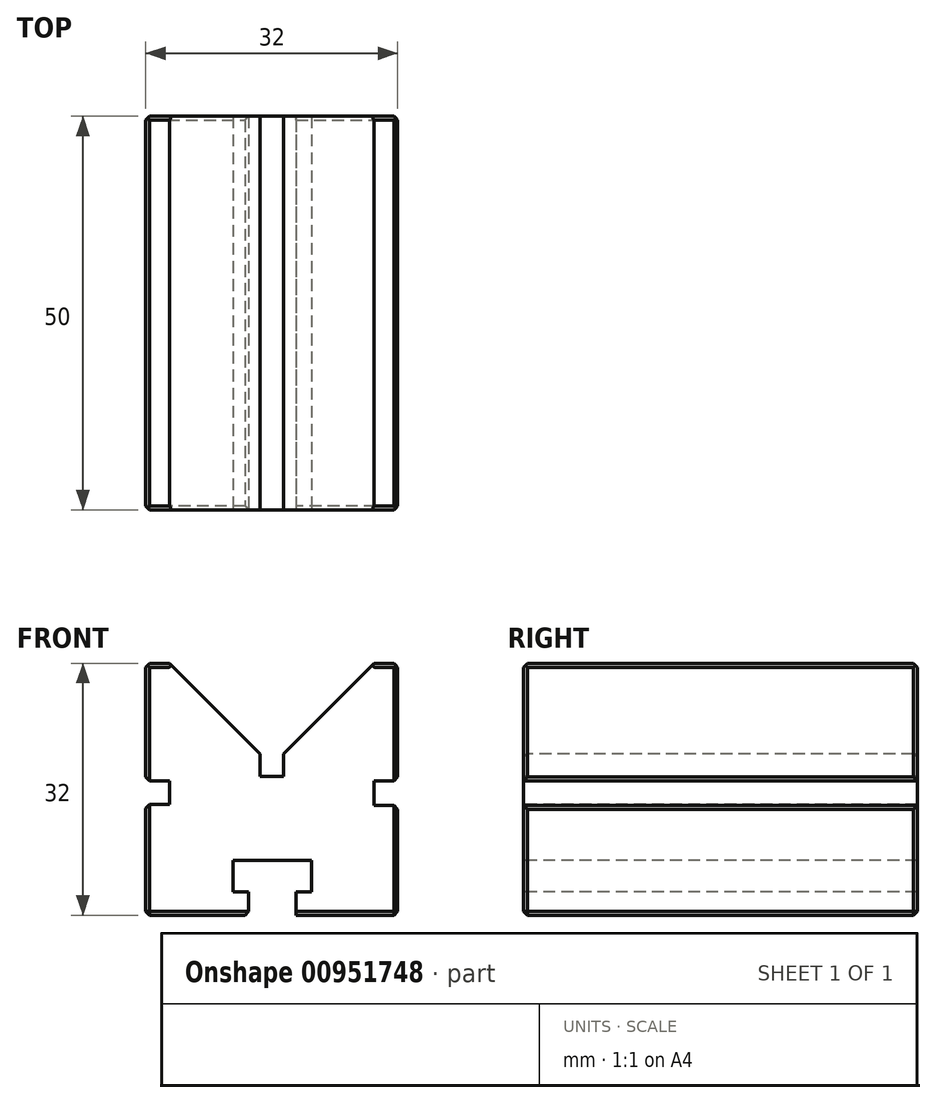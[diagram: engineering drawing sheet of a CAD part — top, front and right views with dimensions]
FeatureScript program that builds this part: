
annotation { "Feature Type Name" : "Feature", "Feature Type Description" : "" }
export const myFeature = defineFeature(function(context is Context, id is Id, definition is map)
    precondition{}
    {
        {
            var Q0;
            Q0=qCreatedBy(makeId("Front.planeOp"),FACE);
            var sketch = newSketch(context, id + "F0", { "sketchPlane" : qUnion([Q0])});
            skLineSegment(sketch, "E0", {"start": v(0, 0) * mm, "end": v(0, 14.06) * mm});
            skLineSegment(sketch, "E1", {"start": v(0, 14.06) * mm, "end": v(3, 14.06) * mm});
            skLineSegment(sketch, "E2", {"start": v(3, 14.06) * mm, "end": v(3, 17.06) * mm});
            skLineSegment(sketch, "E3", {"start": v(3, 17.06) * mm, "end": v(0, 17.06) * mm});
            skLineSegment(sketch, "E4", {"start": v(0, 17.06) * mm, "end": v(0, 32) * mm});
            skLineSegment(sketch, "E5", {"start": v(0, 32) * mm, "end": v(3, 32) * mm});
            skLineSegment(sketch, "E6", {"start": v(3, 32) * mm, "end": v(14.5, 20.5) * mm});
            skLineSegment(sketch, "E7", {"start": v(14.5, 20.5) * mm, "end": v(14.5, 17.62) * mm});
            skLineSegment(sketch, "E8", {"start": v(14.5, 17.62) * mm, "end": v(17.5, 17.62) * mm});
            skLineSegment(sketch, "E9", {"start": v(17.5, 17.62) * mm, "end": v(17.5, 20.5) * mm});
            skLineSegment(sketch, "E10", {"start": v(17.5, 20.5) * mm, "end": v(29, 32) * mm});
            skLineSegment(sketch, "E11", {"start": v(29, 32) * mm, "end": v(32, 32) * mm});
            skLineSegment(sketch, "E12", {"start": v(32, 32) * mm, "end": v(32, 17.06) * mm});
            skLineSegment(sketch, "E13", {"start": v(32, 17.06) * mm, "end": v(29, 17.06) * mm});
            skLineSegment(sketch, "E14", {"start": v(29, 17.06) * mm, "end": v(29, 13.97) * mm});
            skLineSegment(sketch, "E15", {"start": v(29, 13.97) * mm, "end": v(32, 13.97) * mm});
            skLineSegment(sketch, "E16", {"start": v(32, 13.97) * mm, "end": v(32, 0) * mm});
            skLineSegment(sketch, "E17", {"start": v(32, 0) * mm, "end": v(0, 0) * mm});
            skSolve(sketch);
        }
        {
            var Q0;
            Q0=qCreatedBy(makeId("Front.planeOp"),FACE);
            var sketch = newSketch(context, id + "F1", { "sketchPlane" : qUnion([Q0])});
            skLineSegment(sketch, "E18", {"start": v(13.08, 3) * mm, "end": v(11.08, 3) * mm});
            skLineSegment(sketch, "E19", {"start": v(11.08, 3) * mm, "end": v(11.08, 7) * mm});
            skLineSegment(sketch, "E20", {"start": v(11.08, 7) * mm, "end": v(21.08, 7) * mm});
            skLineSegment(sketch, "E21", {"start": v(21.08, 7) * mm, "end": v(21.08, 3) * mm});
            skLineSegment(sketch, "E22", {"start": v(21.08, 3) * mm, "end": v(19.08, 3) * mm});
            skLineSegment(sketch, "E23", {"start": v(13.08, 3) * mm, "end": v(13.08, 0) * mm});
            skLineSegment(sketch, "E24", {"start": v(19.08, 3) * mm, "end": v(19.08, 0) * mm});
            skLineSegment(sketch, "E25", {"start": v(13.08, 0) * mm, "end": v(13.08, -0.7) * mm});
            skLineSegment(sketch, "E26", {"start": v(13.08, -0.7) * mm, "end": v(19, -0.7) * mm});
            skLineSegment(sketch, "E27", {"start": v(19, -0.7) * mm, "end": v(19.08, 0) * mm});
            skSolve(sketch);
        }
        {
            var Q0;
            Q0 = qSketchRegion(id + "F0", true);
            extrude(context, id + "F2", {"entities" : qUnion([Q0]), "oppositeDirection" : true, "depth" : 50 * mm, "offsetDistance" : 25 * mm});
        }
        {
            var Q0;
            Q0 = qSketchRegion(id + "F1", true);
            extrude(context, id + "F3", {"entities" : qUnion([Q0]), "operationType" : NewBodyOperationType.REMOVE, "endBound" : BoundingType.UP_TO_NEXT, "oppositeDirection" : true, "depth" : 55 * mm, "offsetDistance" : 25 * mm});
        }
        {
            var Q0;
            Q0=makeQuery(id+"F2.opExtrude","SWEPT_EDGE",EDGE,{"disambiguationData":[OSD([sQuery(id+"F0.wireOp",EDGE,"E11"),sQuery(id+"F0.wireOp",EDGE,"E12")])]});
            var Q1;
            Q1=makeQuery(id+"F2.opExtrude","SWEPT_EDGE",EDGE,{"disambiguationData":[OSD([sQuery(id+"F0.wireOp",EDGE,"E16"),sQuery(id+"F0.wireOp",EDGE,"E17")])]});
            var Q2;
            Q2=makeQuery(id+"F2.opExtrude","SWEPT_EDGE",EDGE,{"disambiguationData":[OSD([sQuery(id+"F0.wireOp",EDGE,"E4"),sQuery(id+"F0.wireOp",EDGE,"E5")])]});
            var Q3;
            Q3=makeQuery(id+"F2.opExtrude","SWEPT_EDGE",EDGE,{"disambiguationData":[OSD([sQuery(id+"F0.wireOp",EDGE,"E0"),sQuery(id+"F0.wireOp",EDGE,"E17")])]});
            var Q4;
            Q4=makeQuery(id+"F3.boolean.opBoolean","COPY",EDGE,{"derivedFrom":makeQuery(id+"F3.opExtrude","CAP_EDGE",EDGE,{"disambiguationData":[OSD([sQuery(id+"F1.wireOp",EDGE,"E23"),sQuery(id+"F1.wireOp",EDGE,"E25")]),topologyDisambiguationEdgeConnected([makeQuery(id+"F2.opExtrude","SWEPT_FACE",FACE,{"disambiguationData":[OSD([sQuery(id+"F0.wireOp",EDGE,"E17")])]})])],"isStart":false})});
            var Q5;
            Q5=makeQuery(id+"F3.boolean.opBoolean","COPY",EDGE,{"derivedFrom":makeQuery(id+"F3.opExtrude","CAP_EDGE",EDGE,{"disambiguationData":[OSD([sQuery(id+"F1.wireOp",EDGE,"E24")]),topologyDisambiguationEdgeConnected([makeQuery(id+"F2.opExtrude","SWEPT_FACE",FACE,{"disambiguationData":[OSD([sQuery(id+"F0.wireOp",EDGE,"E17")])]})])],"isStart":false})});
            var Q6;
            Q6=makeQuery(id+"F2.opExtrude","SWEPT_EDGE",EDGE,{"disambiguationData":[OSD([sQuery(id+"F0.wireOp",EDGE,"E3"),sQuery(id+"F0.wireOp",EDGE,"E4")])]});
            var Q7;
            Q7=makeQuery(id+"F2.opExtrude","SWEPT_EDGE",EDGE,{"disambiguationData":[OSD([sQuery(id+"F0.wireOp",EDGE,"E0"),sQuery(id+"F0.wireOp",EDGE,"E1")])]});
            var Q8;
            Q8=makeQuery(id+"F2.opExtrude","SWEPT_EDGE",EDGE,{"disambiguationData":[OSD([sQuery(id+"F0.wireOp",EDGE,"E12"),sQuery(id+"F0.wireOp",EDGE,"E13")])]});
            var Q9;
            Q9=makeQuery(id+"F2.opExtrude","SWEPT_EDGE",EDGE,{"disambiguationData":[OSD([sQuery(id+"F0.wireOp",EDGE,"E15"),sQuery(id+"F0.wireOp",EDGE,"E16")])]});
            var Q10;
            Q10=makeQuery(id+"F2.opExtrude","CAP_EDGE",EDGE,{"disambiguationData":[OSD([sQuery(id+"F0.wireOp",EDGE,"E12")])],"isStart":true});
            var Q11;
            Q11=makeQuery(id+"F2.opExtrude","CAP_EDGE",EDGE,{"disambiguationData":[OSD([sQuery(id+"F0.wireOp",EDGE,"E16")])],"isStart":true});
            var Q12;
            Q12=makeQuery(id+"F2.opExtrude","CAP_EDGE",EDGE,{"disambiguationData":[OSD([sQuery(id+"F0.wireOp",EDGE,"E4")])],"isStart":true});
            var Q13;
            Q13=makeQuery(id+"F2.opExtrude","CAP_EDGE",EDGE,{"disambiguationData":[OSD([sQuery(id+"F0.wireOp",EDGE,"E0")])],"isStart":true});
            var Q14;
            Q14=makeQuery(id+"F2.opExtrude","CAP_EDGE",EDGE,{"disambiguationData":[OSD([sQuery(id+"F0.wireOp",EDGE,"E4")])],"isStart":false});
            var Q15;
            Q15=makeQuery(id+"F2.opExtrude","CAP_EDGE",EDGE,{"disambiguationData":[OSD([sQuery(id+"F0.wireOp",EDGE,"E0")])],"isStart":false});
            var Q16;
            Q16=makeQuery(id+"F2.opExtrude","CAP_EDGE",EDGE,{"disambiguationData":[OSD([sQuery(id+"F0.wireOp",EDGE,"E12")])],"isStart":false});
            var Q17;
            Q17=makeQuery(id+"F2.opExtrude","CAP_EDGE",EDGE,{"disambiguationData":[OSD([sQuery(id+"F0.wireOp",EDGE,"E16")])],"isStart":false});
            var Q18;
            {var subQ0=sQuery(id+"F0.wireOp",EDGE,"E17");var subQ1=sQuery(id+"F0.wireOp",EDGE,"E16");Q18=makeQuery(id+"F3.boolean.opBoolean","SPLIT",EDGE,{"disambiguationData":[TD([makeQuery(id+"F2.opExtrude","SWEPT_FACE",FACE,{"disambiguationData":[OSD([subQ1])]})])],"derivedFrom":makeQuery(id+"F2.opExtrude","CAP_EDGE",EDGE,{"disambiguationData":[OSD([subQ0])],"isStart":false})});}
            var Q19;
            {var subQ0=sQuery(id+"F0.wireOp",EDGE,"E0");var subQ1=sQuery(id+"F0.wireOp",EDGE,"E17");Q19=makeQuery(id+"F3.boolean.opBoolean","SPLIT",EDGE,{"disambiguationData":[TD([makeQuery(id+"F2.opExtrude","SWEPT_FACE",FACE,{"disambiguationData":[OSD([subQ0])]})])],"derivedFrom":makeQuery(id+"F2.opExtrude","CAP_EDGE",EDGE,{"disambiguationData":[OSD([subQ1])],"isStart":false})});}
            var Q20;
            {var subQ0=sQuery(id+"F0.wireOp",EDGE,"E0");var subQ1=sQuery(id+"F0.wireOp",EDGE,"E17");Q20=makeQuery(id+"F3.boolean.opBoolean","SPLIT",EDGE,{"disambiguationData":[TD([makeQuery(id+"F2.opExtrude","SWEPT_FACE",FACE,{"disambiguationData":[OSD([subQ0])]})])],"derivedFrom":makeQuery(id+"F2.opExtrude","CAP_EDGE",EDGE,{"disambiguationData":[OSD([subQ1])],"isStart":true})});}
            var Q21;
            {var subQ0=sQuery(id+"F0.wireOp",EDGE,"E17");var subQ1=sQuery(id+"F0.wireOp",EDGE,"E16");Q21=makeQuery(id+"F3.boolean.opBoolean","SPLIT",EDGE,{"disambiguationData":[TD([makeQuery(id+"F2.opExtrude","SWEPT_FACE",FACE,{"disambiguationData":[OSD([subQ1])]})])],"derivedFrom":makeQuery(id+"F2.opExtrude","CAP_EDGE",EDGE,{"disambiguationData":[OSD([subQ0])],"isStart":true})});}
            chamfer(context, id + "F4", {"entities" : qUnion([Q0, Q1, Q2, Q3, Q4, Q5, Q6, Q7, Q8, Q9, Q10, Q11, Q12, Q13, Q14, Q15, Q16, Q17, Q18, Q19, Q20, Q21]), "width" : .5 * mm, "tangentPropagation" : true});
        }
        {
            var Q0;
            Q0=makeQuery(id+"F2.opExtrude","CAP_EDGE",EDGE,{"disambiguationData":[OSD([sQuery(id+"F0.wireOp",EDGE,"E11")])],"isStart":false});
            var Q1;
            Q1=makeQuery(id+"F2.opExtrude","CAP_EDGE",EDGE,{"disambiguationData":[OSD([sQuery(id+"F0.wireOp",EDGE,"E5")])],"isStart":false});
            var Q2;
            Q2=makeQuery(id+"F2.opExtrude","CAP_EDGE",EDGE,{"disambiguationData":[OSD([sQuery(id+"F0.wireOp",EDGE,"E11")])],"isStart":true});
            var Q3;
            Q3=makeQuery(id+"F2.opExtrude","CAP_EDGE",EDGE,{"disambiguationData":[OSD([sQuery(id+"F0.wireOp",EDGE,"E5")])],"isStart":true});
            chamfer(context, id + "F5", {"entities" : qUnion([Q0, Q1, Q2, Q3]), "width" : .5 * mm, "tangentPropagation" : true});
        }
        {
            var Q0;
            Q0=makeQuery(id+"F2.opExtrude","CAP_EDGE",EDGE,{"disambiguationData":[OSD([sQuery(id+"F0.wireOp",EDGE,"E10")])],"isStart":false});
            var Q1;
            Q1=makeQuery(id+"F2.opExtrude","CAP_EDGE",EDGE,{"disambiguationData":[OSD([sQuery(id+"F0.wireOp",EDGE,"E6")])],"isStart":false});
            var Q2;
            Q2=makeQuery(id+"F2.opExtrude","CAP_EDGE",EDGE,{"disambiguationData":[OSD([sQuery(id+"F0.wireOp",EDGE,"E10")])],"isStart":true});
            var Q3;
            Q3=makeQuery(id+"F2.opExtrude","CAP_EDGE",EDGE,{"disambiguationData":[OSD([sQuery(id+"F0.wireOp",EDGE,"E6")])],"isStart":true});
            fillet(context, id + "F6", {"entities" : qUnion([Q0, Q1, Q2, Q3]), "radius" : .5 * mm, "tangentPropagation" : true, "allowEdgeOverflow" : false});
        }
    });
